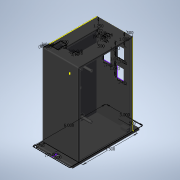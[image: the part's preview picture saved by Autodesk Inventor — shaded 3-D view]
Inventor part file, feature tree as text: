
AUTODESK INVENTOR PART (.ipt)
format: ipt  version: 2020 (Build 240168000, 168)  size: 4,367,360 bytes
history: native  units: in
note: dims shown in document units (in); Inventor stores cm internally (conversion verified against a paired STEP export)
features: sketch x24, extrude x17, hole x5, fillet x3, revolve x3, helix x3, thread x2, pattern_linear x2, other x1
ambient origin geometry x8: Origin, YZ Plane, XZ Plane, XY Plane, X Axis, Y Axis, Z Axis, Center Point
bodies: Solid1 (feature_tree), Solid3 (feature_tree), Solid4 (feature_tree), Solid5 (feature_tree)
feature tree (60):
  sketch  "Sketch1"  dims[d0=3.0in d1=6.0in]
  extrude  "Extrusion1"  Depth=6.0in
  extrude  "Extrusion2"  Depth=4.5in
  hole  "Hole1"  [1 undecoded]
  extrude  "Extrusion7"  Depth=0.1875in
  extrude  "Extrusion8"  Depth=0.1875in
  extrude  "Extrusion3"  Depth=0.125in
  extrude  "Extrusion4"  Depth=0.125in
  extrude  "Extrusion5"  Depth=0.125in TaperAngle=0.0deg
  extrude  "Extrusion6"  Depth=0.25in
  extrude  "Extrusion9"  Depth=0.5in
  hole  "Hole2"  [1 undecoded]
  thread  "Thread1"  [1 undecoded]
  pattern_linear  "Rectangular Pattern1"  Count1=2 Spacing1=1.9291in
  extrude  "Extrusion10"  Depth=0.3937in
  sketch  "Sketch13"  dims[d32=0.25in d33=0.25in d34=0.0in d35=0.5906in]
  hole  "Hole5"  [1 undecoded]
  thread  "Thread3"  [1 undecoded]
  pattern_linear  "Rectangular Pattern2"  Spacing1=0.1875in  [1 undecoded]
  hole  "Hole4"  [1 undecoded]
  fillet  "Fillet1"  Radius=0.125in
  extrude  "Extrusion11"  Depth=0.125in
  extrude  "Extrusion12"  Depth=0.3937in
  sketch  "Sketch18"  dims[d38=2.2835in]
  extrude  "Extrusion13"  Depth=0.3937in
  hole  "Hole6"  [1 undecoded]
  fillet  "Fillet2"  Radius=0.841in
  other  "iFeature13:2"
  sketch  "Sketch20"  dims[d41=0.5in]
  extrude  "Extrusion14"  Depth=0.3937in
  extrude  "Extrusion15"  Depth=0.3937in
  sketch  "Sketch21"  dims[d42=90.0deg]
  extrude  "Extrusion16"  TaperAngle=0.0deg  [1 undecoded]
  extrude  "Extrusion17"  Depth=0.3937in
  fillet  "Fillet3"  Radius=3.0in
  revolve  "Revolution2"  [1 undecoded]
  helix  "Coil2"  [1 undecoded]
  revolve  "Revolution3"  [1 undecoded]
  helix  "Coil3"  [1 undecoded]
  revolve  "Revolution4"  [1 undecoded]
  helix  "Coil4"  [1 undecoded]
  sketch  "Sketch2"  dims[d2=0.75in d3=4.5in]
  sketch  "Sketch3"  dims[d4=0.1875in d5=0.0in d6=6.75in d7=0.0in]
  sketch  "Sketch4"  dims[d8=0.5in]
  sketch  "Sketch5"  dims[d9=0.266in d10=0.75in d11=0.507in d12=0.0625in d13=0.5635in d14=1.0in d15=0.8108in d16=0.1875in]
  sketch  "Sketch6"  dims[d17=0.1875in d18=0.1875in]
  sketch  "Sketch7"  dims[d19=2.8125in d20=0.0in d21=0.125in]
  sketch  "Sketch8"  dims[d22=0.125in d23=0.125in]
  sketch  "Sketch9"  dims[d24=0.125in d25=0.125in d26=0.0in]
  sketch  "Sketch10"  dims[d27=0.5in d28=0.25in]
  sketch  "Sketch12"  dims[d29=0.25in d30=0.0in d31=0.5in]
  sketch  "Sketch16"  dims[d36=0.3937in]
  sketch  "Sketch17"  dims[d37=1.9291in]
  sketch  "Sketch19"  dims[d39=0.25in d40=0.0in]
  sketch  "Sketch24"  dims[d43=0.25in d44=0.0in]
  sketch  "Sketch25"  dims[d45=0.1969in]
  sketch  "Sketch26"  dims[d46=0.25in d47=0.0in]
  sketch  "Sketch27"  dims[d48=0.0807in d49=0.197in d50=0.119in d51=0.188in d52=90.0deg d53=0.25in d54=0.8108in]
  sketch  "Sketch28"  dims[d55=0.25in d56=0.0in d57=0.7874in d59=1.9291in]
  sketch  "Sketch29"  dims[d60=0.7874in d62=2.2835in d63=0.4035in d65=0.8406in d66=0.0in d76=0.7874in d78=2.6772in d79=0.7874in d81=3.6614in d82=0.1875in d83=0.1875in d84=0.125in d85=0.125in d86=0.089in d87=0.146in d88=0.119in d89=0.188in d90=0.5635in d91=0.224in d92=0.8108in d93=0.0625in d94=0.0492in d95=0.1969in d96=0.0807in d97=0.197in d98=0.119in d99=0.188in d100=0.5635in d101=0.259in d102=0.8108in d103=0.841in d104=0.0in d128=2.75in d130=1.5in d131=0.0in d132=1.0in d133=3.0in d134=0.0625in d135=0.0in d136=1.5in d137=0.5in d138=90.0deg d139=0.75in d140=2.75in d141=0.125in d142=0.0in d143=0.375in d144=0.375in d145=0.375in d146=0.375in d147=0.375in d148=0.0in d149=0.1875in d150=0.1875in d151=0.1875in d152=0.1875in d153=0.089in d154=0.197in d155=0.119in d156=0.188in d157=0.5635in d158=0.259in d159=0.8108in d160=0.0625in d161=0.12in d163=0.492in d165=0.129in d167=0.04in d173=1.25in d174=0.75in d175=90.0deg d176=0.4724in d177=0.375in d178=0.0in d179=0.5in d180=1.0in d181=0.748in d182=1.043in d183=0.5in d184=0.748in d185=1.043in d186=0.0197in d187=0.0in d188=0.375in d189=90.0deg d190=0.25in d191=90.0deg d192=0.5in d193=0.75in d194=0.25in d195=0.0in d196=0.0197in d197=0.0in d198=0.125in d206=0.3779in d217=0.3779in d218=0.0028in d219=0.0028in d222=0.0177in d224=0.3779in d226=0.0in d227=0.0177in d228=0.2854in d229=0.3937in d230=0.0in d231=0.0in d232=0.0in d233=0.0in d234=0.0in d235=0.748in d236=1.043in d237=0.3779in d238=0.0028in d239=0.0028in d242=0.0177in d244=0.3779in d246=0.0in d247=0.0177in d248=0.2854in d249=0.3937in d250=0.0in d251=0.0in d252=0.0in d253=0.0in d254=0.0in d255=0.3779in d256=0.0028in d257=0.0028in d260=0.0177in d262=0.3779in d264=0.0in d265=0.0177in d266=0.876in d267=0.3937in d268=0.0in d269=0.0in d270=0.0in d271=0.0in d272=0.0in]
note: 15 required parameter values undecoded (feature->parameter linkage not recoverable at this tier; creation-order binding heuristic only, values carry confidence <= 0.55)